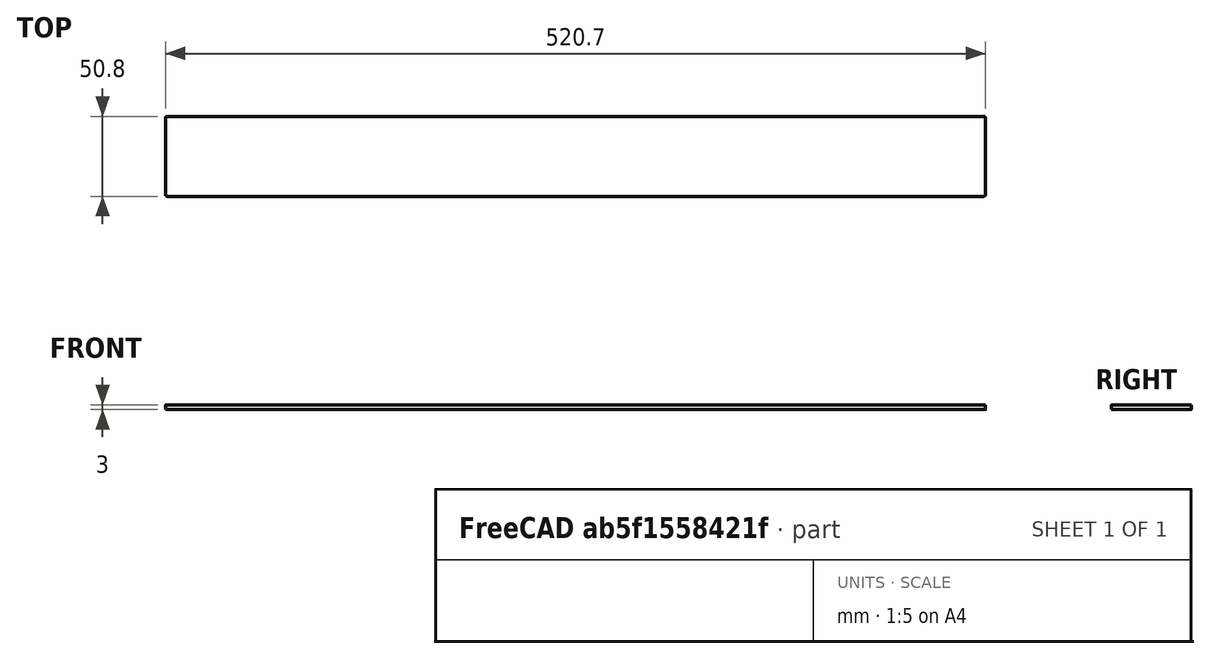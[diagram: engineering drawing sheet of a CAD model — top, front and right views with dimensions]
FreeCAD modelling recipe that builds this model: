
FCSTD DOCUMENT  (FreeCAD 0.20R29603 (Git))
Label: 20p5in_x_2in
License: All rights reserved
LicenseURL: http://en.wikipedia.org/wiki/All_rights_reserved
objects: Spreadsheet::Sheet×1, Sketcher::SketchObject×1, PartDesign::Pad×1, PartDesign::Body×1
note: 4 computed .brp shape members not serialized (recipe doc carries the construction recipe); baked Part::Feature solids carry a one-line shape summary decoded from their .brp

FEATURE [Spreadsheet::Sheet] Spreadsheet
  cells = A2=Length; B2(Length)==20.5in; A3=Width; B3(Width)==2in; A4=Thickness; B4(Thickness)==3mm; A5=FilletRadius; B5(FilletRadius)==1mm
FEATURE [Sketcher::SketchObject] Sketch
  FullyConstrained = true
  MapMode = 5
  Support = -> [XY_Plane]
  expr: Constraints[19] = Spreadsheet.FilletRadius
  expr: Constraints[21] = Spreadsheet.Length
  expr: Constraints[22] = Spreadsheet.Width
  sketch-geometry (10):
    g0: ArcOfCircle CenterX=-259.35 CenterY=24.4 CenterZ=0 NormalX=0 NormalY=0 NormalZ=1 AngleXU=0 Radius=1 StartAngle=1.5708 EndAngle=3.14159
    g1: LineSegment StartX=-259.35 StartY=25.4 StartZ=0 EndX=259.35 EndY=25.4 EndZ=0
    g2: ArcOfCircle CenterX=259.35 CenterY=24.4 CenterZ=0 NormalX=0 NormalY=0 NormalZ=1 AngleXU=0 Radius=1 StartAngle=-5.4481e-12 EndAngle=1.5708
    g3: LineSegment StartX=260.35 StartY=24.4 StartZ=0 EndX=260.35 EndY=-24.4 EndZ=0
    g4: ArcOfCircle CenterX=259.35 CenterY=-24.4 CenterZ=0 NormalX=0 NormalY=0 NormalZ=1 AngleXU=0 Radius=1 StartAngle=4.71239 EndAngle=6.28319
    g5: LineSegment StartX=259.35 StartY=-25.4 StartZ=0 EndX=-259.35 EndY=-25.4 EndZ=0
    g6: ArcOfCircle CenterX=-259.35 CenterY=-24.4 CenterZ=0 NormalX=0 NormalY=0 NormalZ=1 AngleXU=0 Radius=1 StartAngle=3.14159 EndAngle=4.71239
    g7: LineSegment StartX=-260.35 StartY=-24.4 StartZ=0 EndX=-260.35 EndY=24.4 EndZ=0
    g8: GeomPoint X=-260.35 Y=25.4 Z=0
    g9: GeomPoint X=260.35 Y=-25.4 Z=0
  constraints (23):
    c: Tangent(g0,g1) = 1.5708
    c: Tangent(g1,g2) = 1.5708
    c: Tangent(g2,g3) = 1.5708
    c: Tangent(g3,g4) = 1.5708
    c: Tangent(g4,g5) = 1.5708
    c: Tangent(g5,g6) = 1.5708
    c: Tangent(g6,g7) = 1.5708
    c: Tangent(g7,g0) = 1.5708
    c: Horizontal(g1)
    c: Horizontal(g5)
    c: Vertical(g3)
    c: Vertical(g7)
    c: Equal(g0,g2)
    c: Equal(g2,g4)
    c: Equal(g4,g6)
    c: PointOnObject(g8,g1)
    c: PointOnObject(g8,g7)
    c: PointOnObject(g9,g3)
    c: PointOnObject(g9,g5)
    c: Radius(g4) = 1
    c: Symmetric(g8,g9,g-1)
    c: DistanceX(g6,g3) = 520.7
    c: DistanceY(g4,g1) = 50.8
FEATURE [PartDesign::Pad] Pad
  Direction = (0,0,1)
  Length = 3
  Length2 = 10
  Profile = -> Sketch
  ReferenceAxis = -> Sketch [N_Axis]
  Type = 0
  expr: Length = Spreadsheet.Thickness
FEATURE [PartDesign::Body] Body
  Group = -> [Sketch,Pad]
  Origin = -> Origin
  Tip = -> Pad
